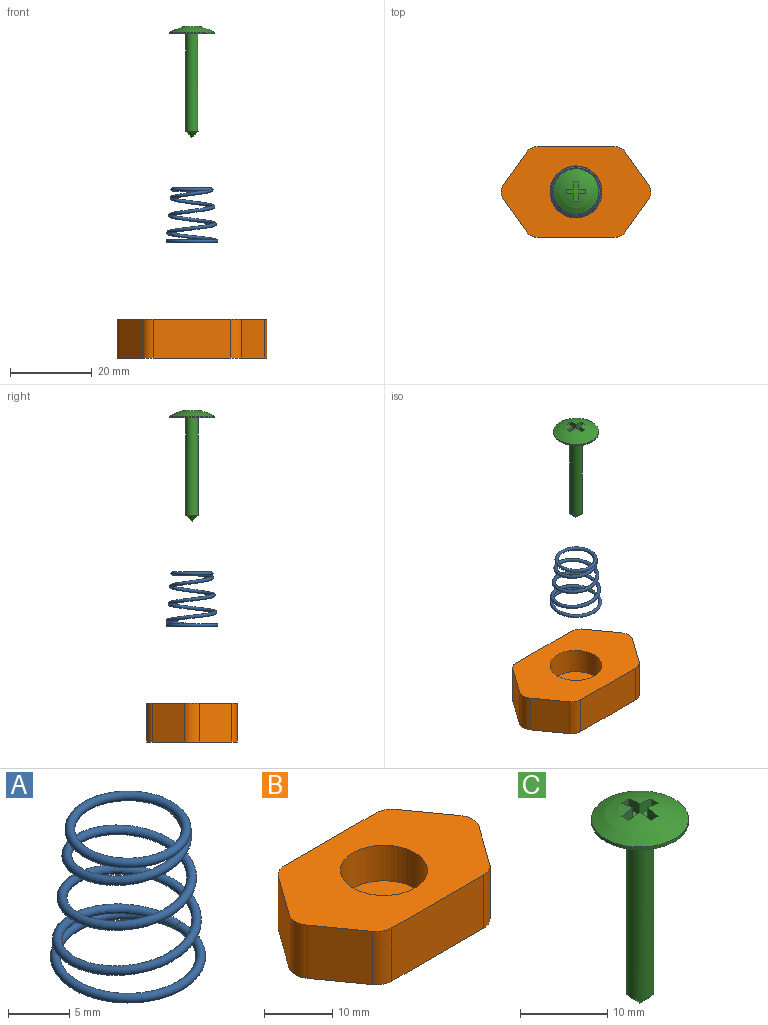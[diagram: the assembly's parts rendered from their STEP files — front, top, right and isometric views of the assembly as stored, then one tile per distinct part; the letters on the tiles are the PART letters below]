
ASSEMBLY  parts=3 mates=2
PART A: 3 faces, bbox 13.7x13.7x13.5 mm
  f0: torus R=4.76mm, axis (0,0,-1), area 70.7mm2, adj f2
  f1: torus R=5.95mm, axis (0,0,-1), area 87.1mm2, adj f2
  f2: bspline ~13.49x12.48mm, area 242.9mm2, adj f0,f1
PART B: 17 faces, bbox 36.6x22.2x9.5 mm
  f0: plane 18.96x9.53mm, normal (0,1,0), area 180.6mm2, adj f7,f8,f11,f16
  f1: plane 9.53x7.94mm, normal (-0.81,0.58,0), area 92.9mm2, adj f7,f8,f11,f12
  f2: plane 9.53x7.94mm, normal (-0.81,-0.58,0), area 92.9mm2, adj f7,f8,f12,f13
  f3: plane 18.96x9.53mm, normal (0,-1,0), area 180.6mm2, adj f7,f8,f13,f14
  f4: plane 9.53x7.94mm, normal (0.81,-0.58,0), area 92.9mm2, adj f7,f8,f14,f15
  f5: cylinder r=6.35mm len=12.7mm, axis (0,0,-1), area 253.4mm2, adj f7,f10
  f6: plane 9.53x7.94mm, normal (0.81,0.58,0), area 92.9mm2, adj f7,f8,f15,f16
  f7: plane 36.65x22.23mm, normal (0,0,1), area 540.2mm2, adj f0,f1,f2,f3,f4,f5,f6,f11
  f8: plane 36.65x22.23mm, normal (0,0,-1), area 649.1mm2, adj f0,f1,f2,f3,f4,f6,f9,f11
  f9: cylinder r=2.38mm len=4.76mm, axis (0,0,-1), area 47.5mm2, adj f8,f10
  f10: plane 12.7x12.7mm, normal (0,0,1), area 108.9mm2, adj f5,f9
  f11: cylinder r=3.17mm len=9.53mm, axis (0,0,-1), area 28.7mm2, adj f0,f1,f7,f8
  f12: cylinder r=3.17mm len=9.53mm, axis (0,0,-1), area 37.5mm2, adj f1,f2,f7,f8
  f13: cylinder r=3.17mm len=9.53mm, axis (0,0,1), area 28.7mm2, adj f2,f3,f7,f8
  f14: cylinder r=3.17mm len=9.53mm, axis (0,0,1), area 28.7mm2, adj f3,f4,f7,f8
  f15: cylinder r=3.17mm len=9.53mm, axis (0,0,-1), area 37.5mm2, adj f4,f6,f7,f8
  f16: cylinder r=3.17mm len=9.53mm, axis (0,0,-1), area 28.7mm2, adj f0,f6,f7,f8
PART C: 18 faces, bbox 11.1x11.1x27.4 mm
  f0: sphere r=10.52mm, area 94.9mm2, adj f1,f5,f6,f7,f8,f9,f10,f11
  f1: cylinder r=5.56mm len=11.11mm, axis (0,0,-1), area 13.9mm2, adj f0,f2
  f2: plane 11.11x11.11mm, normal (0,0,-1), area 89.1mm2, adj f1,f3
  f3: cylinder r=1.59mm len=23.81mm, axis (0,0,-1), area 237.5mm2, adj f2,f4
  f4: cone r=1.59mm half-angle=45deg, axis (0,0,1), area 11.2mm2, adj f3
  f5: plane 1.31x1.19mm, normal (0,-1,0), area 1.6mm2, adj f0,f6,f16,f17
  f6: plane 1.79x1.55mm, normal (1,0,0), area 2.6mm2, adj f0,f5,f7,f17
  f7: plane 1.79x1.55mm, normal (0,-1,0), area 2.6mm2, adj f0,f6,f8,f17
  f8: plane 1.31x1.19mm, normal (1,0,0), area 1.6mm2, adj f0,f7,f9,f17
  f9: plane 1.79x1.55mm, normal (0,1,0), area 2.6mm2, adj f0,f8,f10,f17
  f10: plane 1.79x1.55mm, normal (1,0,0), area 2.6mm2, adj f0,f9,f11,f17
  f11: plane 1.31x1.19mm, normal (0,1,0), area 1.6mm2, adj f0,f10,f12,f17
  f12: plane 1.79x1.55mm, normal (-1,0,0), area 2.6mm2, adj f0,f11,f13,f17
  f13: plane 1.79x1.55mm, normal (0,1,0), area 2.6mm2, adj f0,f12,f14,f17
  f14: plane 1.31x1.19mm, normal (-1,0,0), area 1.6mm2, adj f0,f13,f15,f17
  f15: plane 1.79x1.55mm, normal (0,-1,0), area 2.6mm2, adj f0,f14,f16,f17
  f16: plane 1.79x1.55mm, normal (-1,0,0), area 2.6mm2, adj f0,f5,f15,f17
  f17: plane 4.76x4.76mm, normal (0,0,1), area 9.9mm2, adj f5,f6,f7,f8,f9,f10,f11,f12
PLACE A t=(-7.3,11.38,30.67)mm
PLACE B t=(-7.3,11.38,2.09)mm fixed
PLACE C t=(-38.26,11.38,81.87)mm
MATE fastened B.f5 <-> A.f0  axis (0,0,1) through (-7.3,11.38,5.27)mm
MATE fastened C.f1 <-> A.f0  axis (0,0,-1) through (-7.3,11.38,81.47)mm
